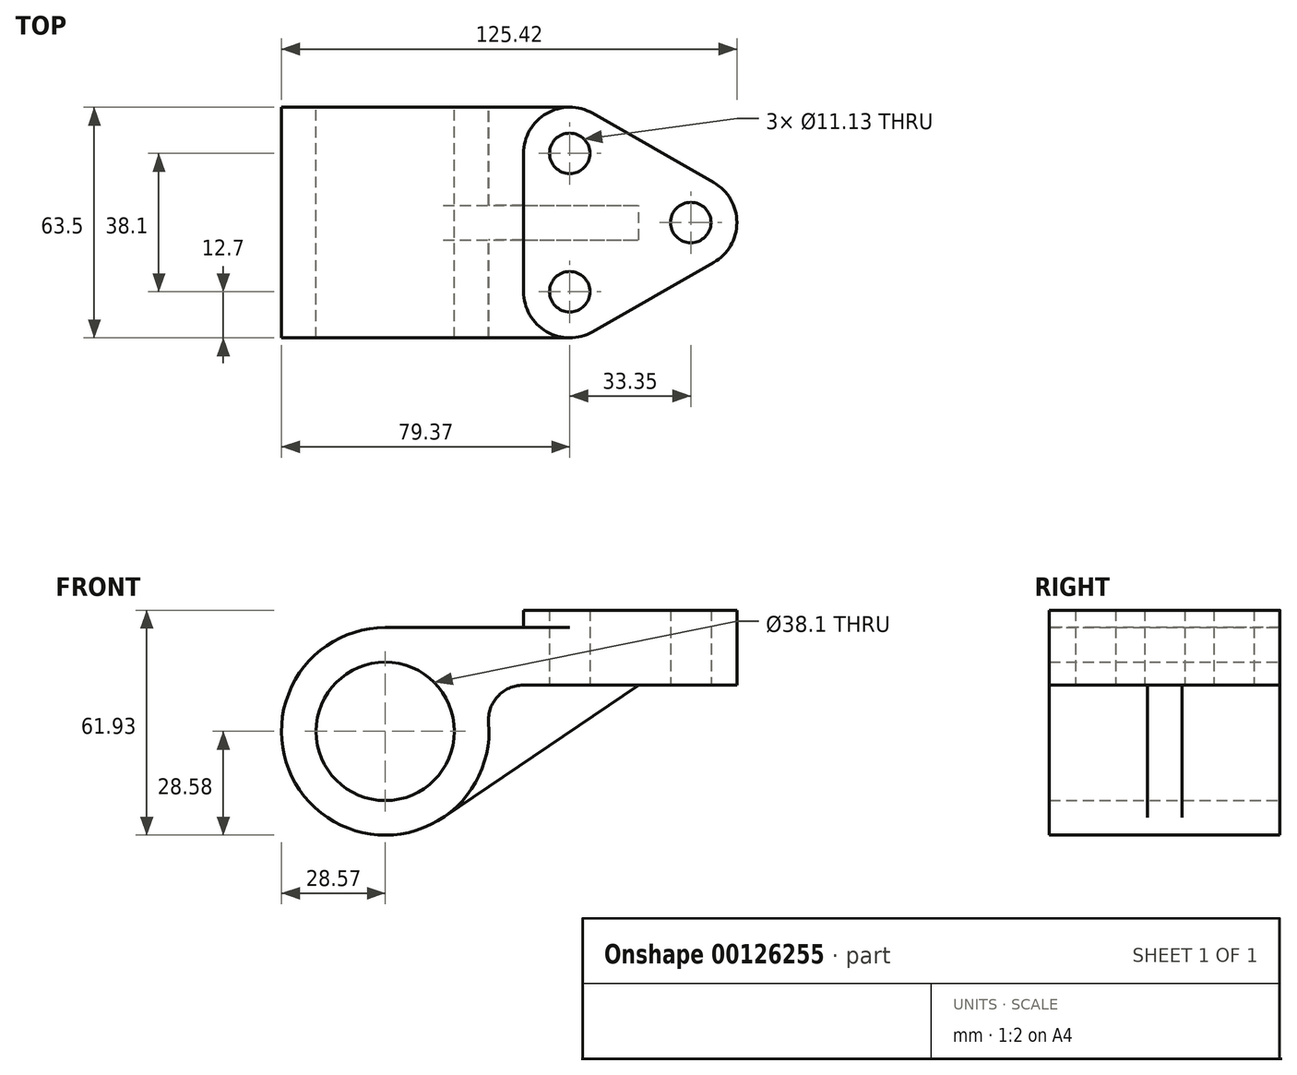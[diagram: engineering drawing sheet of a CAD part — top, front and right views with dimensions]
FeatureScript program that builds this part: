
annotation { "Feature Type Name" : "Feature", "Feature Type Description" : "" }
export const myFeature = defineFeature(function(context is Context, id is Id, definition is map)
    precondition{}
    {
        {
            var Q0;
            Q0=qCreatedBy(makeId("Front.planeOp"),FACE);
            var sketch = newSketch(context, id + "F0", { "sketchPlane" : qUnion([Q0])});
            skCircle(sketch, "E0", {"center": v(0, 0) * mm, "radius": 19.05 * mm});
            skLineSegment(sketch, "E1", {"start": v(0, 28.58) * mm, "end": v(50.8, 28.58) * mm});
            skLineSegment(sketch, "E2", {"start": v(50.8, 28.58) * mm, "end": v(50.8, 12.7) * mm});
            skArc(sketch, "E3", {"start": v(0, 28.58) * mm, "mid": v(-19.35, -21.03) * mm, "end": v(28.48, 2.38) * mm});
            skLineSegment(sketch, "E4", {"start": v(37.97, 12.7) * mm, "end": v(50.8, 12.7) * mm});
            skPoint(sketch, "E5.visualSharp", {"position": v(25.6, 12.7) * mm});
            skArc(sketch, "E5.filletArc", {"start": v(37.97, 12.7) * mm, "mid": v(30.96, 9.62) * mm, "end": v(28.48, 2.38) * mm});
            skSolve(sketch);
        }
        {
            var Q0;
            Q0 = qSketchRegion(id + "F0", true);
            extrude(context, id + "F1", {"entities" : qUnion([Q0]), "depth" : 63.5 * mm, "symmetric" : true});
        }
        {
            var Q0;
            Q0=makeQuery(id+"F1.opExtrude","SWEPT_FACE",FACE,{"disambiguationData":[OSD([sQuery(id+"F0.wireOp",EDGE,"E4")])]});
            var sketch = newSketch(context, id + "F2", { "sketchPlane" : qUnion([Q0])});
            skLineSegment(sketch, "E6", {"start": v(38.1, 19.05) * mm, "end": v(38.1, -19.05) * mm});
            skLineSegment(sketch, "E7", {"start": v(57.1, 30.08) * mm, "end": v(90.45, 11.03) * mm});
            skLineSegment(sketch, "E8", {"start": v(57.1, -30.08) * mm, "end": v(90.45, -11.03) * mm});
            skArc(sketch, "E9", {"start": v(90.45, -11.03) * mm, "mid": v(96.85, 0) * mm, "end": v(90.45, 11.03) * mm});
            skArc(sketch, "E10", {"start": v(57.1, 30.08) * mm, "mid": v(44.42, 30.03) * mm, "end": v(38.1, 19.05) * mm});
            skArc(sketch, "E11", {"start": v(38.1, -19.05) * mm, "mid": v(44.42, -30.03) * mm, "end": v(57.1, -30.08) * mm});
            skCircle(sketch, "E12", {"center": v(50.8, 19.05) * mm, "radius": 5.56 * mm});
            skCircle(sketch, "E13", {"center": v(50.8, -19.05) * mm, "radius": 5.56 * mm});
            skCircle(sketch, "E14", {"center": v(84.15, 0) * mm, "radius": 5.56 * mm});
            skLineSegment(sketch, "E15", {"start": v(0, 0) * mm, "end": v(84.15, 0) * mm, "construction": true});
            skSolve(sketch);
        }
        {
            var Q0;
            {var subQ12=sQuery(id+"F2.wireOp",EDGE,"E7");Q0=makeQuery(id+"F2.imprint","IMPRINT",FACE,{"disambiguationData":[TD([[makeQuery(id+"F2.imprint","IMPRINT",EDGE,{"derivedFrom":subQ12}),-1.0]])]});}
            var Q1;
            {var subQ4=sQuery(id+"F2.wireOp",EDGE,"E6");Q1=makeQuery(id+"F2.imprint","IMPRINT",FACE,{"disambiguationData":[TD([[makeQuery(id+"F2.imprint","IMPRINT",EDGE,{"derivedFrom":subQ4}),1.0]])]});}
            extrude(context, id + "F3", {"entities" : qUnion([Q0, Q1]), "operationType" : NewBodyOperationType.ADD, "oppositeDirection" : true, "depth" : 20.65 * mm});
        }
        {
            var Q0;
            Q0=makeQuery(id+"F3.boolean.opBoolean","SPLIT",FACE,{"disambiguationData":[TD([makeQuery(id+"F3.opExtrude","SWEPT_FACE",FACE,{"disambiguationData":[OSD([sQuery(id+"F2.wireOp",EDGE,"E13")])]})])],"derivedFrom":makeQuery(id+"F1.opExtrude","SWEPT_FACE",FACE,{"disambiguationData":[OSD([sQuery(id+"F0.wireOp",EDGE,"E1")])]})});
            var Q1;
            Q1=makeQuery(id+"F3.boolean.opBoolean","SPLIT",FACE,{"disambiguationData":[TD([makeQuery(id+"F3.opExtrude","SWEPT_FACE",FACE,{"disambiguationData":[OSD([sQuery(id+"F2.wireOp",EDGE,"E12")])]})])],"derivedFrom":makeQuery(id+"F1.opExtrude","SWEPT_FACE",FACE,{"disambiguationData":[OSD([sQuery(id+"F0.wireOp",EDGE,"E1")])]})});
            extrude(context, id + "F4", {"entities" : qUnion([Q0, Q1]), "operationType" : NewBodyOperationType.REMOVE, "endBound" : BoundingType.THROUGH_ALL, "oppositeDirection" : true, "depth" : 25.4 * mm});
        }
        {
            var Q0;
            Q0=qCreatedBy(makeId("Front.planeOp"),FACE);
            var sketch = newSketch(context, id + "F5", { "sketchPlane" : qUnion([Q0])});
            skLineSegment(sketch, "E16", {"start": v(16, -23.68) * mm, "end": v(69.85, 12.7) * mm});
            skArc(sketch, "E17.0", {"start": v(16, -23.68) * mm, "mid": v(25.77, -12.34) * mm, "end": v(28.48, 2.38) * mm});
            skArc(sketch, "E18.0", {"start": v(37.97, 12.7) * mm, "mid": v(30.96, 9.62) * mm, "end": v(28.48, 2.38) * mm});
            skLineSegment(sketch, "E19.0", {"start": v(37.97, 12.7) * mm, "end": v(50.8, 12.7) * mm});
            skLineSegment(sketch, "E20.0", {"start": v(57.1, 12.7) * mm, "end": v(50.8, 12.7) * mm});
            skLineSegment(sketch, "E21.0", {"start": v(57.1, 12.7) * mm, "end": v(69.85, 12.7) * mm});
            skPoint(sketch, "E22.orphan", {"position": v(0, 28.58) * mm});
            skPoint(sketch, "E23.orphan", {"position": v(90.45, 12.7) * mm});
            skSolve(sketch);
        }
        {
            var Q0;
            Q0=makeQuery(id+"F5.imprint","IMPRINT",FACE,{"disambiguationData":[TD([[makeQuery(id+"F5.imprint","IMPRINT",EDGE,{"derivedFrom":sQuery(id+"F5.wireOp",EDGE,"E16")}),1.0]])]});
            extrude(context, id + "F6", {"entities" : qUnion([Q0]), "operationType" : NewBodyOperationType.ADD, "depth" : 9.52 * mm, "symmetric" : true});
        }
    });
